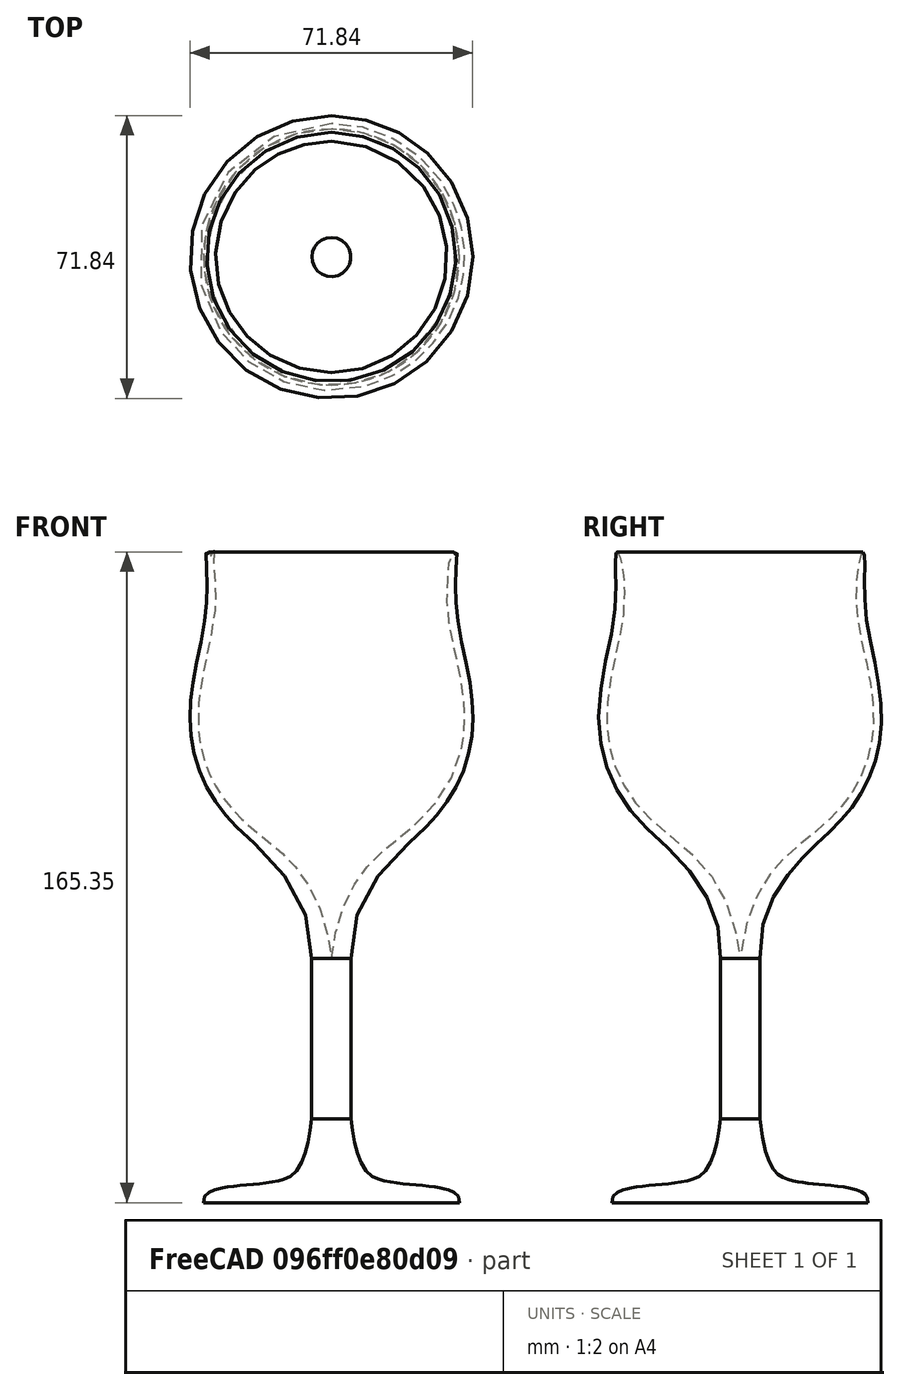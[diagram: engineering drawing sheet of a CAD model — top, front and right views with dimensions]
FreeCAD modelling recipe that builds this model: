
FCSTD DOCUMENT  (FreeCAD 0.19R24276 (Git))
Label: Glass_max_2
License: All rights reserved
LicenseURL: http://en.wikipedia.org/wiki/All_rights_reserved
objects: Sketcher::SketchObject×1, PartDesign::Revolution×1, PartDesign::Body×1
note: 4 computed .brp shape members not serialized (recipe doc carries the construction recipe); baked Part::Feature solids carry a one-line shape summary decoded from their .brp

FEATURE [Sketcher::SketchObject] Sketch003
  FullyConstrained = false
  MapMode = 5
  Placement = pos=(0,0,0) rot=(0.57735,0.57735,0.57735;2.0944rad)
  Support = -> [YZ_Plane]
  sketch-geometry (51):
    g0: LineSegment StartX=33.3721 StartY=129.989 StartZ=0 EndX=35.464 EndY=129.989 EndZ=0
    g1: LineSegment StartX=-50.3421 StartY=166 StartZ=0 EndX=30.3178 EndY=166 EndZ=0
    g2-g19: Circle x18 (B-spline internal-alignment scaffolding for g20; pole/knot coordinates omitted)
    g20: BSplineCurve PolesCount=18 KnotsCount=16 Degree=3 IsPeriodic=0
    g21-g36: GeomPoint x16 (B-spline internal-alignment scaffolding for g20; pole/knot coordinates omitted)
    g37: LineSegment StartX=0 StartY=62.0982 StartZ=0 EndX=0 EndY=0 EndZ=0
    g38: LineSegment StartX=5 StartY=62 StartZ=0 EndX=5 EndY=21.338 EndZ=0
    g39-g44: Circle x6 (B-spline internal-alignment scaffolding for g45; pole/knot coordinates omitted)
    g45: BSplineCurve PolesCount=6 KnotsCount=4 Degree=3 IsPeriodic=0
    g46-g49: GeomPoint x4 (B-spline internal-alignment scaffolding for g45; pole/knot coordinates omitted)
    g50: LineSegment StartX=0 StartY=0 StartZ=0 EndX=32.5 EndY=0 EndZ=0
  constraints (21):
    c: Horizontal(g1)
    c: Horizontal(g0)
    c: DistanceY(g-1,g1) = 166
    c: PointOnObject(g20,g-2)
    c: Weight(g2) = 1
    c: Equal(g2, g3-g19) x17
    c: InternalAlignment(g2-g19 -> g20) x18
    c: InternalAlignment(g21-g36 -> g20) x16
    c: Coincident(g37,g20)
    c: Coincident(g38,g20)
    c: Vertical(g38)
    c: Coincident(g45,g38)
    c: Weight(g39) = 1
    c: Equal(g39, g40-g44) x5
    c: PointOnObject(g45,g-1)
    c: InternalAlignment(g39-g44 -> g45) x6
    c: InternalAlignment(g46-g49 -> g45) x4
    c: DistanceX(g-1,g38) = 5
    c: DistanceX(g-1,g44) = 32.5
    c: Coincident(g50,g-1)
    c: Coincident(g50,g44)
FEATURE [PartDesign::Revolution] Revolution
  Angle = 360
  Axis = (-2e-16,3e-16,1)
  Base = (0,0,0)
  Placement = pos=(0,0,0) rot=(0.57735,0.57735,0.57735;2.0944rad)
  Profile = -> Sketch003
  ReferenceAxis = -> Sketch003 [V_Axis]
  Reversed = true
FEATURE [PartDesign::Body] Body
  Group = -> [Sketch003,Revolution]
  Origin = -> Origin
  Tip = -> Revolution
